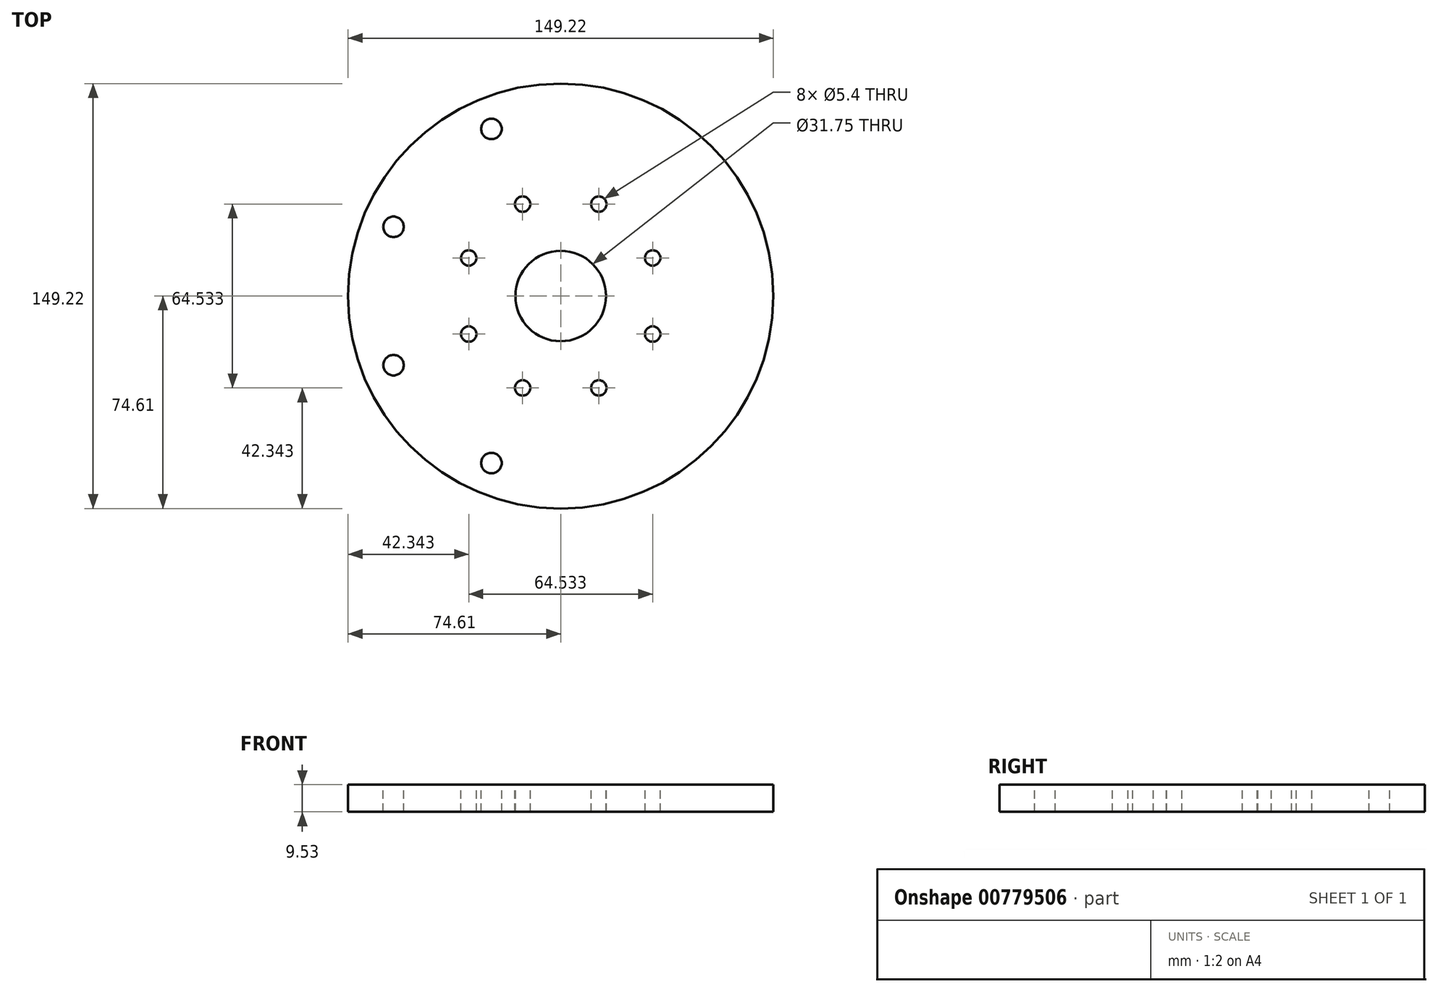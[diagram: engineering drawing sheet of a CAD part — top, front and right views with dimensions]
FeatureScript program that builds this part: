
annotation { "Feature Type Name" : "Feature", "Feature Type Description" : "" }
export const myFeature = defineFeature(function(context is Context, id is Id, definition is map)
    precondition{}
    {
        {
            var Q0;
            Q0=qCreatedBy(makeId("Top.planeOp"),FACE);
            var sketch = newSketch(context, id + "F0", { "sketchPlane" : qUnion([Q0])});
            skCircle(sketch, "E0", {"center": v(0, 0) * mm, "radius": 74.61 * mm});
            skSolve(sketch);
        }
        {
            var Q0;
            Q0=makeQuery(id+"F0.imprint","IMPRINT",FACE,{"disambiguationData":[TD([[makeQuery(id+"F0.imprint","IMPRINT",EDGE,{"derivedFrom":sQuery(id+"F0.wireOp",EDGE,"E0")}),1.0]])]});
            extrude(context, id + "F1", {"entities" : qUnion([Q0]), "depth" : 9.52 * mm, "offsetDistance" : 25.4 * mm});
        }
        {
            var Q0;
            Q0=makeQuery(id+"F1.opExtrude","CAP_FACE",FACE,{"disambiguationData":[OSD([sQuery(id+"F0.wireOp",EDGE,"E0")])],"isStart":false});
            var sketch = newSketch(context, id + "F2", { "sketchPlane" : qUnion([Q0])});
            skCircle(sketch, "E1", {"center": v(0, 0) * mm, "radius": 15.88 * mm});
            skSolve(sketch);
        }
        {
            var Q0;
            Q0=makeQuery(id+"F2.imprint","IMPRINT",FACE,{"disambiguationData":[TD([[makeQuery(id+"F2.imprint","IMPRINT",EDGE,{"derivedFrom":sQuery(id+"F2.wireOp",EDGE,"E1")}),1.0]])]});
            extrude(context, id + "F3", {"entities" : qUnion([Q0]), "operationType" : NewBodyOperationType.REMOVE, "endBound" : BoundingType.THROUGH_ALL, "oppositeDirection" : true, "depth" : 25.4 * mm, "offsetDistance" : 25.4 * mm});
        }
        {
            var Q0;
            Q0=makeQuery(id+"F1.opExtrude","CAP_FACE",FACE,{"disambiguationData":[OSD([sQuery(id+"F0.wireOp",EDGE,"E0")])],"isStart":false});
            var sketch = newSketch(context, id + "F4", { "sketchPlane" : qUnion([Q0])});
            skPoint(sketch, "E2", {"position": v(-32.27, -13.37) * mm});
            skPoint(sketch, "E3.1.0", {"position": v(-13.37, -32.27) * mm});
            skPoint(sketch, "E3.2.0", {"position": v(13.37, -32.27) * mm});
            skPoint(sketch, "E3.3.0", {"position": v(32.27, -13.37) * mm});
            skPoint(sketch, "E3.4.0", {"position": v(32.27, 13.37) * mm});
            skPoint(sketch, "E3.5.0", {"position": v(13.37, 32.27) * mm});
            skPoint(sketch, "E3.6.0", {"position": v(-13.37, 32.27) * mm});
            skPoint(sketch, "E3.7.0", {"position": v(-32.27, 13.37) * mm});
            skPoint(sketch, "E3.center", {"position": v(0, 0) * mm});
            skSolve(sketch);
        }
        {
            var Q0;
            Q0=sQuery(id+"F4.wireOp",VERTEX,"E3.6.0");
            var Q1;
            Q1=sQuery(id+"F4.wireOp",VERTEX,"E3.7.0");
            var Q2;
            Q2=sQuery(id+"F4.wireOp",VERTEX,"E2");
            var Q3;
            Q3=sQuery(id+"F4.wireOp",VERTEX,"E3.1.0");
            var Q4;
            Q4=sQuery(id+"F4.wireOp",VERTEX,"E3.2.0");
            var Q5;
            Q5=sQuery(id+"F4.wireOp",VERTEX,"E3.3.0");
            var Q6;
            Q6=sQuery(id+"F4.wireOp",VERTEX,"E3.4.0");
            var Q7;
            Q7=sQuery(id+"F4.wireOp",VERTEX,"E3.5.0");
            var Q8;
            Q8=makeQuery(id+"F1.opExtrude","SWEPT_BODY",BODY,{"disambiguationData":[OSD([sQuery(id+"F0.wireOp",EDGE,"E0")])]});
            hole(context, id + "F5", {"style" : HoleStyle.SIMPLE, "endStyle" : HoleEndStyle.THROUGH, "standardTappedOrClearance" : lookupTablePath({ "standard" : "ISO", "engagement" : "50%", "pitch" : "1 mm", "size" : "M6", "type" : "Tapped" }), "standardBlindInLast" : lookupTablePath({ "standard" : "ISO", "engagement" : "50%", "pitch" : "1 mm", "size" : "M6", "type" : "Tapped" }), "holeDiameter" : 5.4 * mm, "majorDiameter" : 6 * mm, "showTappedDepth" : true, "isTappedThrough" : true, "tappedDepth" : 3.63 * mm, "tapClearance" : 3, "startFromSketch" : true, "locations" : qUnion([Q0, Q1, Q2, Q3, Q4, Q5, Q6, Q7]), "scope" : qUnion([Q8])});
        }
        {
            var Q0;
            Q0=makeQuery(id+"F1.opExtrude","CAP_FACE",FACE,{"disambiguationData":[OSD([sQuery(id+"F0.wireOp",EDGE,"E0")])],"isStart":false});
            var sketch = newSketch(context, id + "F6", { "sketchPlane" : qUnion([Q0])});
            skLineSegment(sketch, "E4.bottom", {"start": v(0, 88.49) * mm, "end": v(92, 88.49) * mm});
            skLineSegment(sketch, "E4.top", {"start": v(0, -93.4) * mm, "end": v(92, -93.4) * mm});
            skLineSegment(sketch, "E4.left", {"start": v(0, 88.49) * mm, "end": v(0, -93.4) * mm});
            skLineSegment(sketch, "E4.right", {"start": v(92, 88.49) * mm, "end": v(92, -93.4) * mm});
            skSolve(sketch);
        }
        {
            var Q0;
            {var subQ1=sQuery(id+"F6.wireOp",EDGE,"E4.bottom");Q0=makeQuery(id+"F6.imprint","IMPRINT",FACE,{"disambiguationData":[TD([[makeQuery(id+"F6.imprint","IMPRINT",EDGE,{"derivedFrom":subQ1}),-1.0]])]});}
            var Q1;
            Q1=makeQuery(id+"F6.imprint","IMPRINT",FACE,{"disambiguationData":[TD([[makeQuery(id+"F6.imprint","IMPRINT",EDGE,{"derivedFrom":makeQuery(id+"F5.hole-4.boolean.opBoolean","COPY",EDGE,{"derivedFrom":makeQuery(id+"F5.hole-4.opRevolve","SWEPT_EDGE",EDGE,{"disambiguationData":[OSD([sQuery(id+"F5.hole-4.sketch.wireOp",EDGE,"core_line_2"),sQuery(id+"F5.hole-4.sketch.wireOp",EDGE,"core_line_3")])]})})}),-1.0]])]});
            extrude(context, id + "F7", {"entities" : qUnion([Q0, Q1]), "operationType" : NewBodyOperationType.REMOVE, "endBound" : BoundingType.THROUGH_ALL, "oppositeDirection" : true, "depth" : 25.4 * mm, "offsetDistance" : 25.4 * mm});
        }
        {
            var Q0;
            Q0=makeQuery(id+"F1.opExtrude","CAP_FACE",FACE,{"disambiguationData":[OSD([sQuery(id+"F0.wireOp",EDGE,"E0")])],"isStart":false});
            var sketch = newSketch(context, id + "F8", { "sketchPlane" : qUnion([Q0])});
            skPoint(sketch, "E5", {"position": v(-58.67, -24.3) * mm});
            skPoint(sketch, "E6.1.0", {"position": v(-24.3, -58.67) * mm});
            skPoint(sketch, "E6.2.0", {"position": v(24.3, -58.67) * mm});
            skPoint(sketch, "E6.3.0", {"position": v(58.67, -24.3) * mm});
            skPoint(sketch, "E6.4.0", {"position": v(58.67, 24.3) * mm});
            skPoint(sketch, "E6.5.0", {"position": v(24.3, 58.67) * mm});
            skPoint(sketch, "E6.6.0", {"position": v(-24.3, 58.67) * mm});
            skPoint(sketch, "E6.7.0", {"position": v(-58.67, 24.3) * mm});
            skPoint(sketch, "E6.center", {"position": v(0, 0) * mm});
            skSolve(sketch);
        }
        {
            var Q0;
            Q0=sQuery(id+"F8.wireOp",VERTEX,"E6.6.0");
            var Q1;
            Q1=sQuery(id+"F8.wireOp",VERTEX,"E6.7.0");
            var Q2;
            Q2=sQuery(id+"F8.wireOp",VERTEX,"E5");
            var Q3;
            Q3=sQuery(id+"F8.wireOp",VERTEX,"E6.1.0");
            var Q4;
            Q4=makeQuery(id+"F1.opExtrude","SWEPT_BODY",BODY,{"disambiguationData":[OSD([sQuery(id+"F0.wireOp",EDGE,"E0")])]});
            hole(context, id + "F9", {"style" : HoleStyle.SIMPLE, "endStyle" : HoleEndStyle.THROUGH, "standardTappedOrClearance" : lookupTablePath({ "standard" : "ISO", "engagement" : "50%", "pitch" : "1.25 mm", "size" : "M8", "type" : "Tapped" }), "standardBlindInLast" : lookupTablePath({ "standard" : "ISO", "engagement" : "50%", "pitch" : "1.25 mm", "size" : "M8", "type" : "Tapped" }), "holeDiameter" : 7.2 * mm, "majorDiameter" : 8 * mm, "showTappedDepth" : true, "isTappedThrough" : true, "tappedDepth" : 3.63 * mm, "tapClearance" : 3, "startFromSketch" : true, "locations" : qUnion([Q0, Q1, Q2, Q3]), "scope" : qUnion([Q4])});
        }
    });
